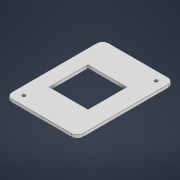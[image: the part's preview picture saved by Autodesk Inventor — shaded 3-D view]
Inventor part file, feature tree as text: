
AUTODESK INVENTOR PART (.ipt)
format: ipt  version: 2022 (Build 260153000, 153)  size: 109,056 bytes
history: native  units: in
note: dims shown in document units (in); Inventor stores cm internally (conversion verified against a paired STEP export)
features: extrude x1, sketch x1
ambient origin geometry x8: Origin, YZ Plane, XZ Plane, XY Plane, X Axis, Y Axis, Z Axis, Center Point
bodies: Solid1 (feature_tree)
feature tree (2):
  extrude  "Extrusion1"  Depth=2.5591in
  sketch  "Sketch1"  dims[d0=1.8898in d1=2.5591in d3=0.1575in d17=0.0787in d18=0.0in d19=0.0197in d20=0.0344in]
